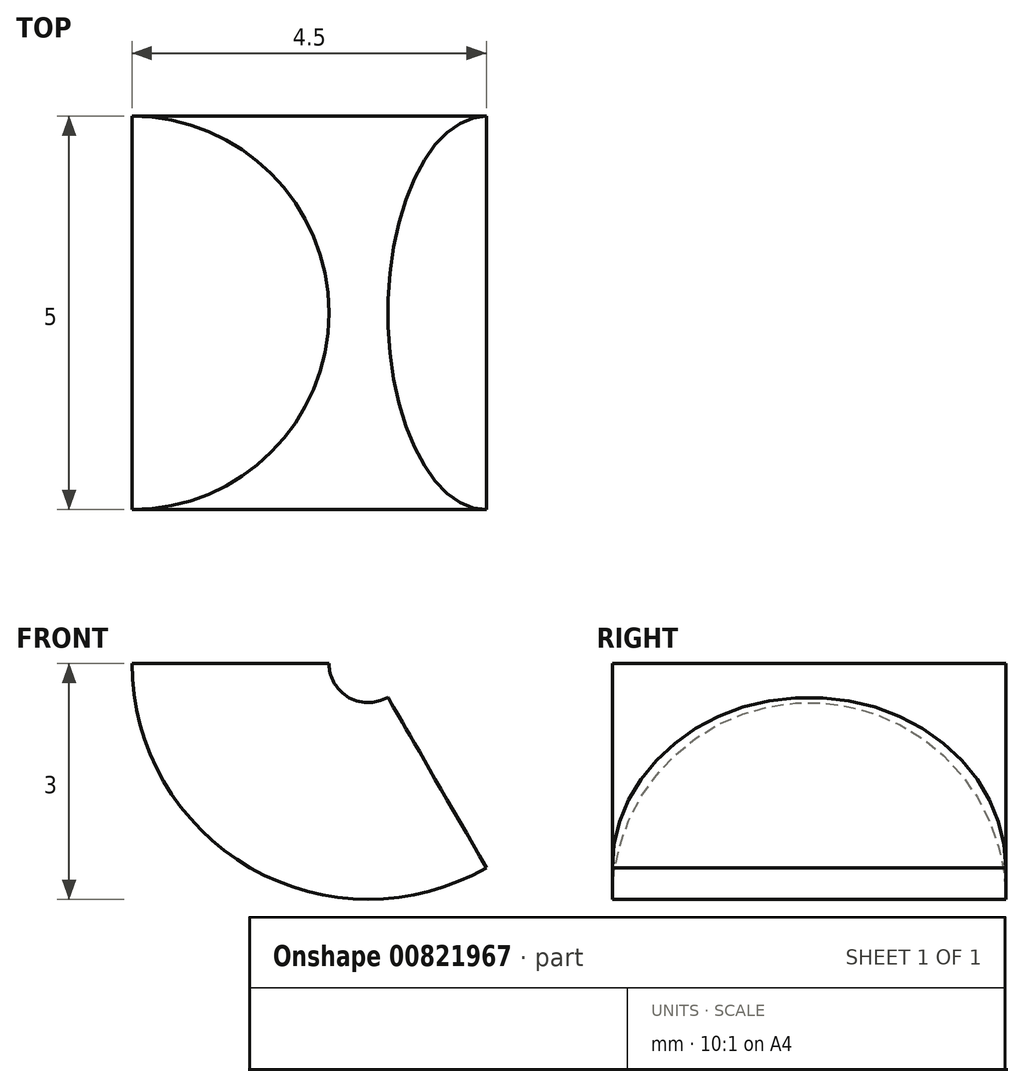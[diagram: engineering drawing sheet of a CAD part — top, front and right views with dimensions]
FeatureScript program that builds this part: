
annotation { "Feature Type Name" : "Feature", "Feature Type Description" : "" }
export const myFeature = defineFeature(function(context is Context, id is Id, definition is map)
    precondition{}
    {
        {
            var Q0;
            Q0=qCreatedBy(makeId("Top.planeOp"),FACE);
            var sketch = newSketch(context, id + "F0", { "sketchPlane" : qUnion([Q0])});
            skLineSegment(sketch, "E0", {"start": v(2.42, 0) * mm, "end": v(2.42, -5) * mm});
            skArc(sketch, "E1", {"start": v(2.42, -5) * mm, "mid": v(4.92, -2.5) * mm, "end": v(2.42, 0) * mm});
            skLineSegment(sketch, "E2", {"start": v(2.42, 0) * mm, "end": v(4.92, 0) * mm});
            skLineSegment(sketch, "E3", {"start": v(4.92, 0) * mm, "end": v(5.42, 0) * mm});
            skLineSegment(sketch, "E4", {"start": v(5.42, 0) * mm, "end": v(5.42, -15.32) * mm});
            skSolve(sketch);
        }
        {
            var Q0;
            Q0=qSketchRegion(id+"F0",true);
            var Q1;
            Q1=sQuery(id+"F0.wireOp",EDGE,"E4");
            revolve(context, id + "F1", {"surfaceOperationType" : NewSurfaceOperationType.NEW, "entities" : qUnion([Q0]), "axis" : qUnion([Q1]), "revolveType" : RevolveType.ONE_DIRECTION, "angle" : 120 * degree});
        }
    });
